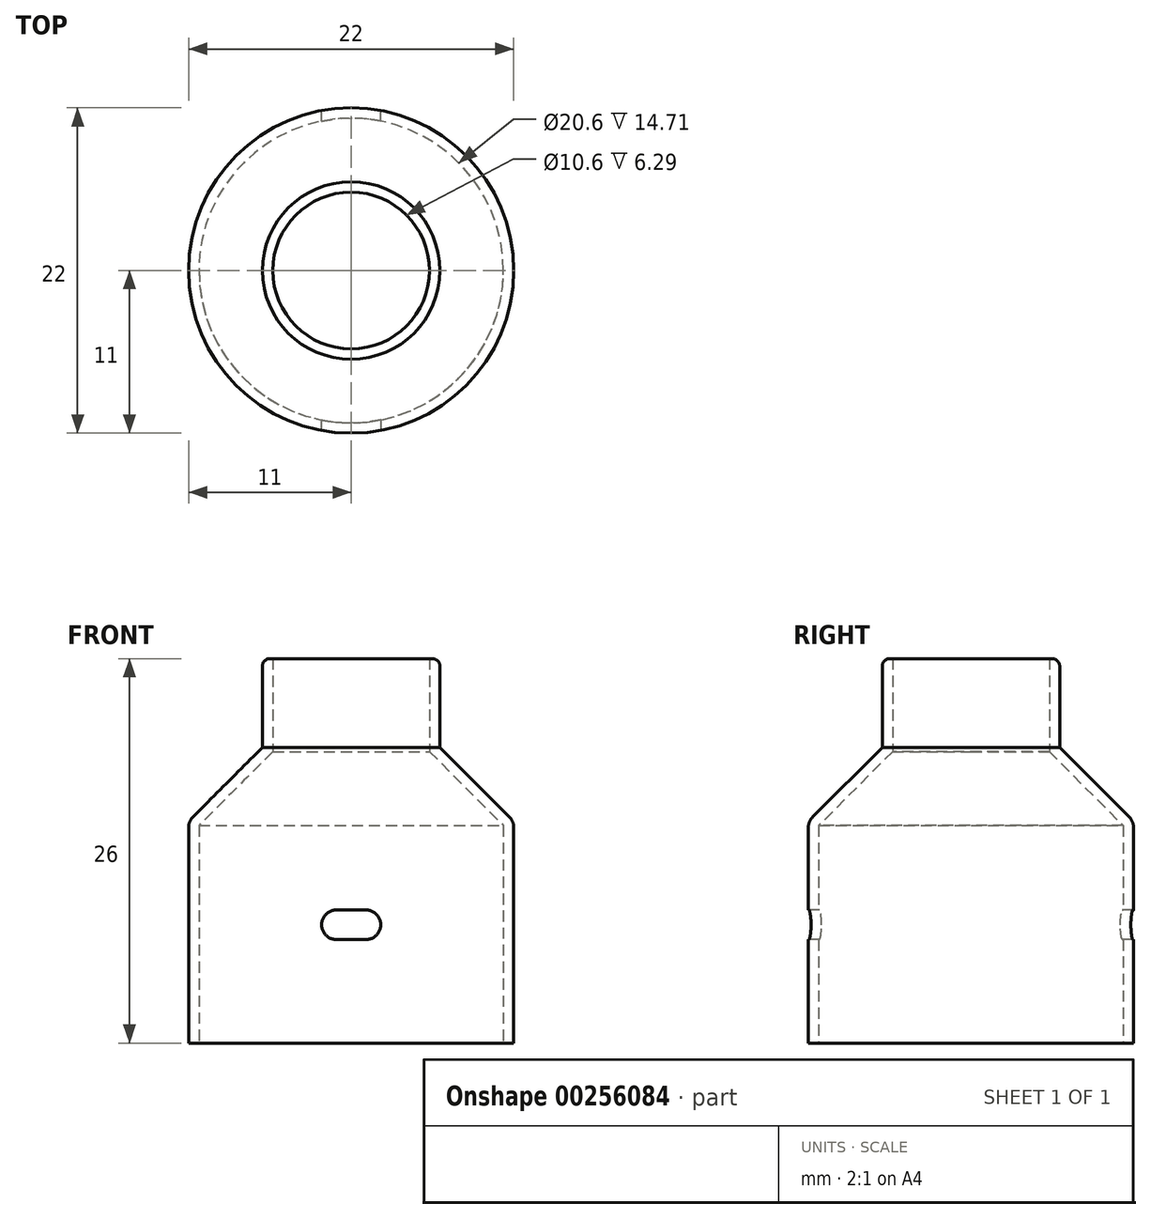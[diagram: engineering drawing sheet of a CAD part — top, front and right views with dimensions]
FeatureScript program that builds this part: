
annotation { "Feature Type Name" : "Feature", "Feature Type Description" : "" }
export const myFeature = defineFeature(function(context is Context, id is Id, definition is map)
    precondition{}
    {
        {
            var Q0;
            Q0=qCreatedBy(makeId("Top.planeOp"),FACE);
            var sketch = newSketch(context, id + "F0", { "sketchPlane" : qUnion([Q0])});
            skCircle(sketch, "E0", {"center": v(0, 0) * mm, "radius": 11 * mm});
            skSolve(sketch);
        }
        {
            var Q0;
            Q0=makeQuery(id+"F0.imprint","IMPRINT",FACE,{"disambiguationData":[TD([[makeQuery(id+"F0.imprint","IMPRINT",EDGE,{"derivedFrom":sQuery(id+"F0.wireOp",EDGE,"E0")}),1.0]])]});
            extrude(context, id + "F1", {"entities" : qUnion([Q0]), "depth" : 20 * mm});
        }
        {
            var Q0;
            Q0=makeQuery(id+"F1.opExtrude","CAP_EDGE",EDGE,{"disambiguationData":[OSD([sQuery(id+"F0.wireOp",EDGE,"E0")])],"isStart":false});
            chamfer(context, id + "F2", {"entities" : qUnion([Q0]), "width" : 5 * mm, "tangentPropagation" : true});
        }
        {
            var Q0;
            Q0=makeQuery(id+"F1.opExtrude","CAP_FACE",FACE,{"disambiguationData":[OSD([sQuery(id+"F0.wireOp",EDGE,"E0")])],"isStart":false});
            extrude(context, id + "F3", {"entities" : qUnion([Q0]), "operationType" : NewBodyOperationType.ADD, "depth" : 6 * mm});
        }
        {
            var Q0;
            Q0=makeQuery(id+"F3.opExtrude","CAP_FACE",FACE,{"disambiguationData":[OSD([sQuery(id+"F0.wireOp",EDGE,"E0")])],"isStart":false});
            var Q1;
            Q1=makeQuery(id+"F1.opExtrude","CAP_FACE",FACE,{"disambiguationData":[OSD([sQuery(id+"F0.wireOp",EDGE,"E0")])],"isStart":true});
            shell(context, id + "F4", {"entities" : qUnion([Q0, Q1]), "thickness" : .7 * mm});
        }
        {
            var Q0;
            Q0=qCreatedBy(makeId("Front.planeOp"),FACE);
            var sketch = newSketch(context, id + "F5", { "sketchPlane" : qUnion([Q0])});
            skLineSegment(sketch, "E1.bottom", {"start": v(2, 7) * mm, "end": v(-2, 7) * mm});
            skLineSegment(sketch, "E1.top", {"start": v(2, 9) * mm, "end": v(-2, 9) * mm});
            skLineSegment(sketch, "E1.left", {"start": v(2, 7) * mm, "end": v(2, 9) * mm});
            skLineSegment(sketch, "E1.right", {"start": v(-2, 7) * mm, "end": v(-2, 9) * mm});
            skPoint(sketch, "E1.middle", {"position": v(0, 8) * mm});
            skSolve(sketch);
        }
        {
            var Q0;
            Q0 = qSketchRegion(id + "F5", true);
            extrude(context, id + "F6", {"entities" : qUnion([Q0]), "operationType" : NewBodyOperationType.REMOVE, "endBound" : BoundingType.SYMMETRIC, "oppositeDirection" : true, "depth" : 25 * mm});
        }
        {
            var Q0;
            Q0=makeQuery(id+"F6.boolean.opBoolean","COPY",EDGE,{"disambiguationData":[OD(1.0)],"derivedFrom":makeQuery(id+"F6.opExtrude","SWEPT_EDGE",EDGE,{"disambiguationData":[OSD([sQuery(id+"F5.wireOp",EDGE,"E1.bottom"),sQuery(id+"F5.wireOp",EDGE,"E1.right")])]})});
            var Q1;
            Q1=makeQuery(id+"F6.boolean.opBoolean","COPY",EDGE,{"disambiguationData":[OD(1.0)],"derivedFrom":makeQuery(id+"F6.opExtrude","SWEPT_EDGE",EDGE,{"disambiguationData":[OSD([sQuery(id+"F5.wireOp",EDGE,"E1.top"),sQuery(id+"F5.wireOp",EDGE,"E1.left")])]})});
            var Q2;
            Q2=makeQuery(id+"F6.boolean.opBoolean","COPY",EDGE,{"disambiguationData":[OD(1.0)],"derivedFrom":makeQuery(id+"F6.opExtrude","SWEPT_EDGE",EDGE,{"disambiguationData":[OSD([sQuery(id+"F5.wireOp",EDGE,"E1.top"),sQuery(id+"F5.wireOp",EDGE,"E1.right")])]})});
            var Q3;
            Q3=makeQuery(id+"F6.boolean.opBoolean","COPY",EDGE,{"disambiguationData":[OD(1.0)],"derivedFrom":makeQuery(id+"F6.opExtrude","SWEPT_EDGE",EDGE,{"disambiguationData":[OSD([sQuery(id+"F5.wireOp",EDGE,"E1.bottom"),sQuery(id+"F5.wireOp",EDGE,"E1.left")])]})});
            var Q4;
            Q4=makeQuery(id+"F6.boolean.opBoolean","COPY",EDGE,{"disambiguationData":[OD(0.0)],"derivedFrom":makeQuery(id+"F6.opExtrude","SWEPT_EDGE",EDGE,{"disambiguationData":[OSD([sQuery(id+"F5.wireOp",EDGE,"E1.bottom"),sQuery(id+"F5.wireOp",EDGE,"E1.right")])]})});
            var Q5;
            Q5=makeQuery(id+"F6.boolean.opBoolean","COPY",EDGE,{"disambiguationData":[OD(0.0)],"derivedFrom":makeQuery(id+"F6.opExtrude","SWEPT_EDGE",EDGE,{"disambiguationData":[OSD([sQuery(id+"F5.wireOp",EDGE,"E1.top"),sQuery(id+"F5.wireOp",EDGE,"E1.right")])]})});
            var Q6;
            Q6=makeQuery(id+"F6.boolean.opBoolean","COPY",EDGE,{"disambiguationData":[OD(0.0)],"derivedFrom":makeQuery(id+"F6.opExtrude","SWEPT_EDGE",EDGE,{"disambiguationData":[OSD([sQuery(id+"F5.wireOp",EDGE,"E1.bottom"),sQuery(id+"F5.wireOp",EDGE,"E1.left")])]})});
            var Q7;
            Q7=makeQuery(id+"F6.boolean.opBoolean","COPY",EDGE,{"disambiguationData":[OD(0.0)],"derivedFrom":makeQuery(id+"F6.opExtrude","SWEPT_EDGE",EDGE,{"disambiguationData":[OSD([sQuery(id+"F5.wireOp",EDGE,"E1.top"),sQuery(id+"F5.wireOp",EDGE,"E1.left")])]})});
            fillet(context, id + "F7", {"entities" : qUnion([Q0, Q1, Q2, Q3, Q4, Q5, Q6, Q7]), "radius" : 1 * mm, "tangentPropagation" : true, "allowEdgeOverflow" : false});
        }
        {
            var Q0;
            Q0=makeQuery(id+"F3.opExtrude","CAP_EDGE",EDGE,{"disambiguationData":[OSD([sQuery(id+"F0.wireOp",EDGE,"E0")])],"isStart":false});
            fillet(context, id + "F8", {"entities" : qUnion([Q0]), "radius" : .5 * mm, "tangentPropagation" : true, "allowEdgeOverflow" : false});
        }
        {
            var Q0;
            {var subQ0=sQuery(id+"F0.wireOp",EDGE,"E0");Q0=makeQuery(id+"F2.opChamfer","BLEND_EDGE",EDGE,{"blendedFrom":[makeQuery(id+"F1.opExtrude","CAP_EDGE",EDGE,{"disambiguationData":[OSD([subQ0])],"isStart":false}),makeQuery(id+"F1.opExtrude","SWEPT_FACE",FACE,{"disambiguationData":[OSD([subQ0])]})],"blendedInto":[makeQuery(id+"F1.opExtrude","SWEPT_FACE",FACE,{"disambiguationData":[OSD([subQ0])]})]});}
            fillet(context, id + "F9", {"entities" : qUnion([Q0]), "radius" : 1 * mm, "tangentPropagation" : true, "allowEdgeOverflow" : false});
        }
    });
